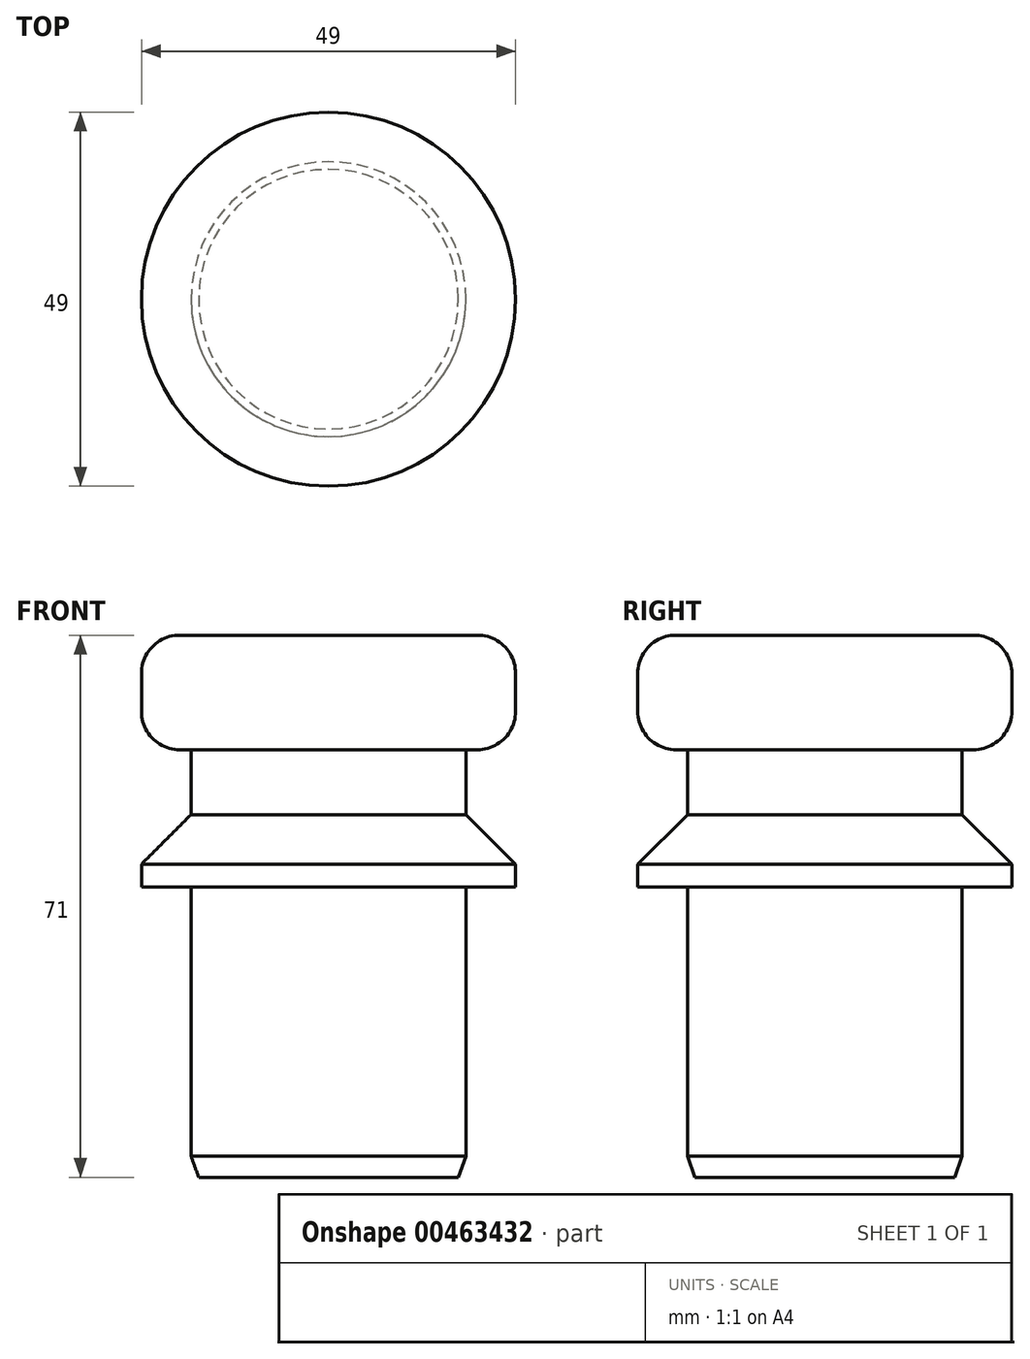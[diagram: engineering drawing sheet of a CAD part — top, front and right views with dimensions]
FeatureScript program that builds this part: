
annotation { "Feature Type Name" : "Feature", "Feature Type Description" : "" }
export const myFeature = defineFeature(function(context is Context, id is Id, definition is map)
    precondition{}
    {
        {
            var Q0;
            Q0=qCreatedBy(makeId("Front.planeOp"),FACE);
            var sketch = newSketch(context, id + "F0", { "sketchPlane" : qUnion([Q0])});
            skLineSegment(sketch, "E0", {"start": v(0, 0) * mm, "end": v(-18, 0) * mm});
            skLineSegment(sketch, "E1", {"start": v(-18, 0) * mm, "end": v(-18, 38) * mm});
            skLineSegment(sketch, "E2", {"start": v(-18, 38) * mm, "end": v(-24.5, 38) * mm});
            skLineSegment(sketch, "E3", {"start": v(0, 0) * mm, "end": v(0, 71) * mm});
            skLineSegment(sketch, "E4", {"start": v(-24.5, 38) * mm, "end": v(-24.5, 41) * mm});
            skLineSegment(sketch, "E5", {"start": v(-24.5, 41) * mm, "end": v(-18, 41) * mm});
            skLineSegment(sketch, "E6", {"start": v(-18, 41) * mm, "end": v(-18, 56) * mm});
            skLineSegment(sketch, "E7", {"start": v(-18, 56) * mm, "end": v(-24.5, 56) * mm});
            skLineSegment(sketch, "E8", {"start": v(-24.5, 56) * mm, "end": v(-24.5, 71) * mm});
            skLineSegment(sketch, "E9", {"start": v(-24.5, 71) * mm, "end": v(0, 71) * mm});
            skSolve(sketch);
        }
        {
            var Q0;
            Q0=makeQuery(id+"F0.imprint","IMPRINT",FACE,{"disambiguationData":[TD([[makeQuery(id+"F0.imprint","IMPRINT",EDGE,{"derivedFrom":sQuery(id+"F0.wireOp",EDGE,"E0")}),-1.0]])]});
            var Q1;
            Q1=sQuery(id+"F0.wireOp",EDGE,"E3");
            revolve(context, id + "F1", {"entities" : qUnion([Q0]), "axis" : qUnion([Q1]), "revolveType" : RevolveType.FULL});
        }
        {
            var Q0;
            Q0=makeQuery(id+"F1.opRevolve","SWEPT_EDGE",EDGE,{"disambiguationData":[OSD([sQuery(id+"F0.wireOp",EDGE,"E7"),sQuery(id+"F0.wireOp",EDGE,"E8")])]});
            var Q1;
            Q1=makeQuery(id+"F1.opRevolve","SWEPT_EDGE",EDGE,{"disambiguationData":[OSD([sQuery(id+"F0.wireOp",EDGE,"E8"),sQuery(id+"F0.wireOp",EDGE,"E9")])]});
            fillet(context, id + "F2", {"entities" : qUnion([Q0, Q1]), "radius" : 5 * mm, "tangentPropagation" : true, "allowEdgeOverflow" : false});
        }
        {
            var Q0;
            Q0=makeQuery(id+"F1.opRevolve","SWEPT_EDGE",EDGE,{"disambiguationData":[OSD([sQuery(id+"F0.wireOp",EDGE,"E5"),sQuery(id+"F0.wireOp",EDGE,"E6")])]});
            chamfer(context, id + "F3", {"entities" : qUnion([Q0]), "width" : 6.5 * mm, "tangentPropagation" : true});
        }
        {
            var Q0;
            Q0=makeQuery(id+"F1.opRevolve","SWEPT_EDGE",EDGE,{"disambiguationData":[OSD([sQuery(id+"F0.wireOp",EDGE,"E0"),sQuery(id+"F0.wireOp",EDGE,"E1")])]});
            chamfer(context, id + "F4", {"entities" : qUnion([Q0]), "chamferType" : ChamferType.OFFSET_ANGLE, "width" : 1 * mm, "oppositeDirection" : false, "angle" : 70 * degree, "tangentPropagation" : true});
        }
    });
